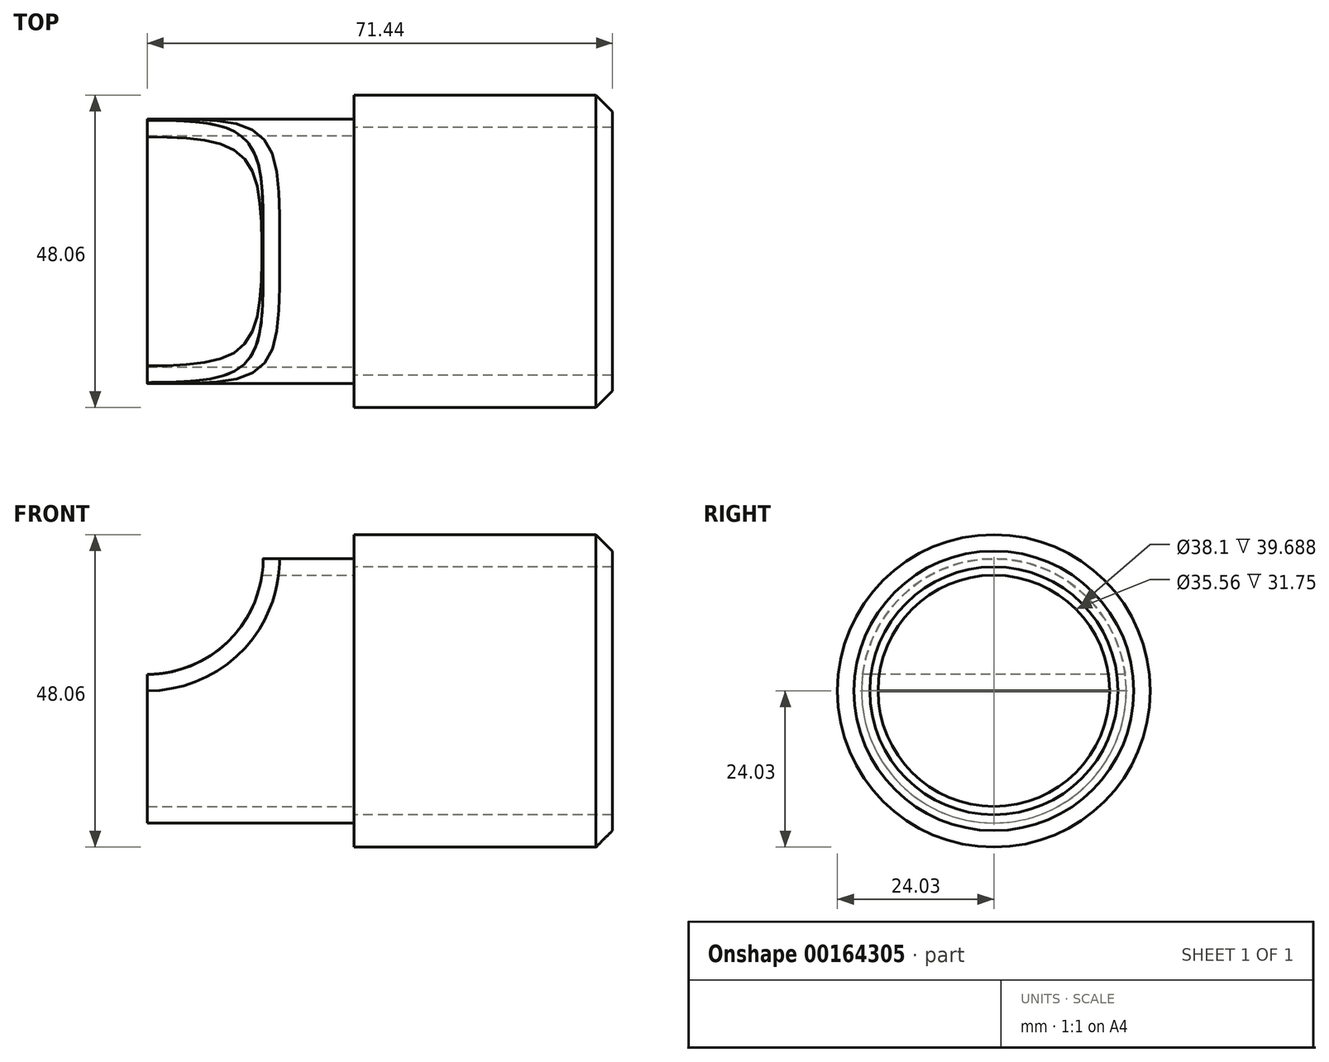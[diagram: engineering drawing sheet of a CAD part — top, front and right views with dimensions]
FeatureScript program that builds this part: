
annotation { "Feature Type Name" : "Feature", "Feature Type Description" : "" }
export const myFeature = defineFeature(function(context is Context, id is Id, definition is map)
    precondition{}
    {
        {
            var Q0;
            Q0=qCreatedBy(makeId("Right.planeOp"),FACE);
            var sketch = newSketch(context, id + "F0", { "sketchPlane" : qUnion([Q0])});
            skCircle(sketch, "E0", {"center": v(0, 0) * mm, "radius": 19.05 * mm});
            skCircle(sketch, "E1", {"center": v(0, 0) * mm, "radius": 24.03 * mm});
            skSolve(sketch);
        }
        {
            var Q0;
            Q0 = qSketchRegion(id + "F0", true);
            extrude(context, id + "F1", {"entities" : qUnion([Q0]), "depth" : 39.69 * mm});
        }
        {
            var Q0;
            Q0=qCreatedBy(makeId("Front.planeOp"),FACE);
            var sketch = newSketch(context, id + "F2", { "sketchPlane" : qUnion([Q0])});
            skLineSegment(sketch, "E2", {"start": v(0, 0) * mm, "end": v(39.69, 0) * mm, "construction": true});
            skLineSegment(sketch, "E3", {"start": v(39.69, 0) * mm, "end": v(39.69, 24.03) * mm, "construction": true});
            skLineSegment(sketch, "E4", {"start": v(39.69, 24.03) * mm, "end": v(37.15, 24.03) * mm});
            skLineSegment(sketch, "E5", {"start": v(37.15, 24.03) * mm, "end": v(39.69, 21.49) * mm});
            skLineSegment(sketch, "E6", {"start": v(39.69, 21.49) * mm, "end": v(39.69, 24.03) * mm});
            skSolve(sketch);
        }
        {
            var Q0;
            Q0=makeQuery(id+"F2.imprint","IMPRINT",FACE,{"disambiguationData":[TD([[makeQuery(id+"F2.imprint","IMPRINT",EDGE,{"derivedFrom":sQuery(id+"F2.wireOp",EDGE,"E4")}),1.0]])]});
            var Q1;
            Q1=sQuery(id+"F2.wireOp",EDGE,"E2");
            revolve(context, id + "F3", {"operationType" : NewBodyOperationType.REMOVE, "entities" : qUnion([Q0]), "axis" : qUnion([Q1]), "revolveType" : RevolveType.FULL, "oppositeDirection" : true});
        }
        {
            var Q0;
            Q0=qCreatedBy(makeId("Right.planeOp"),FACE);
            var sketch = newSketch(context, id + "F4", { "sketchPlane" : qUnion([Q0])});
            skCircle(sketch, "E7", {"center": v(0, 0) * mm, "radius": 24.03 * mm});
            skCircle(sketch, "E8", {"center": v(0, 0) * mm, "radius": 20.32 * mm});
            skCircle(sketch, "E9", {"center": v(0, 0) * mm, "radius": 17.78 * mm});
            skSolve(sketch);
        }
        {
            var Q0;
            Q0 = qSketchRegion(id + "F4", true);
            var Q1;
            Q1=makeQuery(id+"F4.imprint","IMPRINT",FACE,{"disambiguationData":[TD([[makeQuery(id+"F4.imprint","IMPRINT",EDGE,{"derivedFrom":sQuery(id+"F4.wireOp",EDGE,"E8")}),1.0]])]});
            extrude(context, id + "F5", {"entities" : qUnion([Q0, Q1]), "oppositeDirection" : true, "depth" : 2.54 * mm});
        }
        {
            var Q0;
            Q0=makeQuery(id+"F4.imprint","IMPRINT",FACE,{"disambiguationData":[TD([[makeQuery(id+"F4.imprint","IMPRINT",EDGE,{"derivedFrom":sQuery(id+"F4.wireOp",EDGE,"E8")}),1.0]])]});
            extrude(context, id + "F6", {"entities" : qUnion([Q0]), "operationType" : NewBodyOperationType.ADD, "oppositeDirection" : true, "depth" : 31.75 * mm});
        }
        {
            var Q0;
            Q0=qCreatedBy(makeId("Front.planeOp"),FACE);
            var sketch = newSketch(context, id + "F7", { "sketchPlane" : qUnion([Q0])});
            skLineSegment(sketch, "E10", {"start": v(0, 0) * mm, "end": v(-31.75, 0) * mm, "construction": true});
            skLineSegment(sketch, "E11", {"start": v(-31.75, 0) * mm, "end": v(-31.75, 20.32) * mm, "construction": true});
            skCircle(sketch, "E12", {"center": v(-31.75, 20.32) * mm, "radius": 20.32 * mm});
            skCircle(sketch, "E13", {"center": v(-31.75, 20.32) * mm, "radius": 17.78 * mm});
            skSolve(sketch);
        }
        {
            var Q0;
            Q0 = qSketchRegion(id + "F7", true);
            extrude(context, id + "F8", {"entities" : qUnion([Q0]), "oppositeDirection" : true, "depth" : 25.4 * mm, "hasSecondDirection" : true, "secondDirectionOppositeDirection" : false, "secondDirectionDepth" : 25.4 * mm});
        }
        {
            var Q0;
            Q0=qCreatedBy(makeId("Front.planeOp"),FACE);
            var sketch = newSketch(context, id + "F9", { "sketchPlane" : qUnion([Q0])});
            skLineSegment(sketch, "E14", {"start": v(0, 0) * mm, "end": v(-31.75, 0) * mm, "construction": true});
            skLineSegment(sketch, "E15", {"start": v(-31.75, 0) * mm, "end": v(-31.75, 20.32) * mm});
            skArc(sketch, "E16", {"start": v(-31.75, 0) * mm, "mid": v(-46.12, 34.69) * mm, "end": v(-11.43, 20.32) * mm});
            skLineSegment(sketch, "E17", {"start": v(-31.75, 20.32) * mm, "end": v(-11.43, 20.32) * mm});
            skSolve(sketch);
        }
        {
            var Q0;
            Q0=makeQuery(id+"F9.imprint","IMPRINT",FACE,{"disambiguationData":[TD([[makeQuery(id+"F9.imprint","IMPRINT",EDGE,{"derivedFrom":sQuery(id+"F9.wireOp",EDGE,"E15")}),1.0]])]});
            extrude(context, id + "F10", {"entities" : qUnion([Q0]), "operationType" : NewBodyOperationType.REMOVE, "oppositeDirection" : true, "depth" : 25.4 * mm, "hasSecondDirection" : true, "secondDirectionOppositeDirection" : false, "secondDirectionDepth" : 25.4 * mm});
        }
        {
            var Q0;
            Q0=qCreatedBy(makeId("Right.planeOp"),FACE);
            var sketch = newSketch(context, id + "F11", { "sketchPlane" : qUnion([Q0])});
            skCircle(sketch, "E18", {"center": v(0, 0) * mm, "radius": 20.32 * mm});
            skCircle(sketch, "E19", {"center": v(0, 0) * mm, "radius": 41.56 * mm});
            skSolve(sketch);
        }
        {
            var Q0;
            Q0 = qSketchRegion(id + "F11", true);
            extrude(context, id + "F12", {"entities" : qUnion([Q0]), "operationType" : NewBodyOperationType.REMOVE, "oppositeDirection" : true, "depth" : 50.8 * mm});
        }
        {
            var Q0;
            Q0=makeQuery(id+"F7.imprint","IMPRINT",FACE,{"disambiguationData":[TD([[makeQuery(id+"F7.imprint","IMPRINT",EDGE,{"derivedFrom":sQuery(id+"F7.wireOp",EDGE,"E13")}),1.0]])]});
            extrude(context, id + "F13", {"entities" : qUnion([Q0]), "operationType" : NewBodyOperationType.REMOVE, "oppositeDirection" : true, "depth" : 25.4 * mm, "hasSecondDirection" : true, "secondDirectionOppositeDirection" : false, "secondDirectionDepth" : 25.4 * mm});
        }
    });
